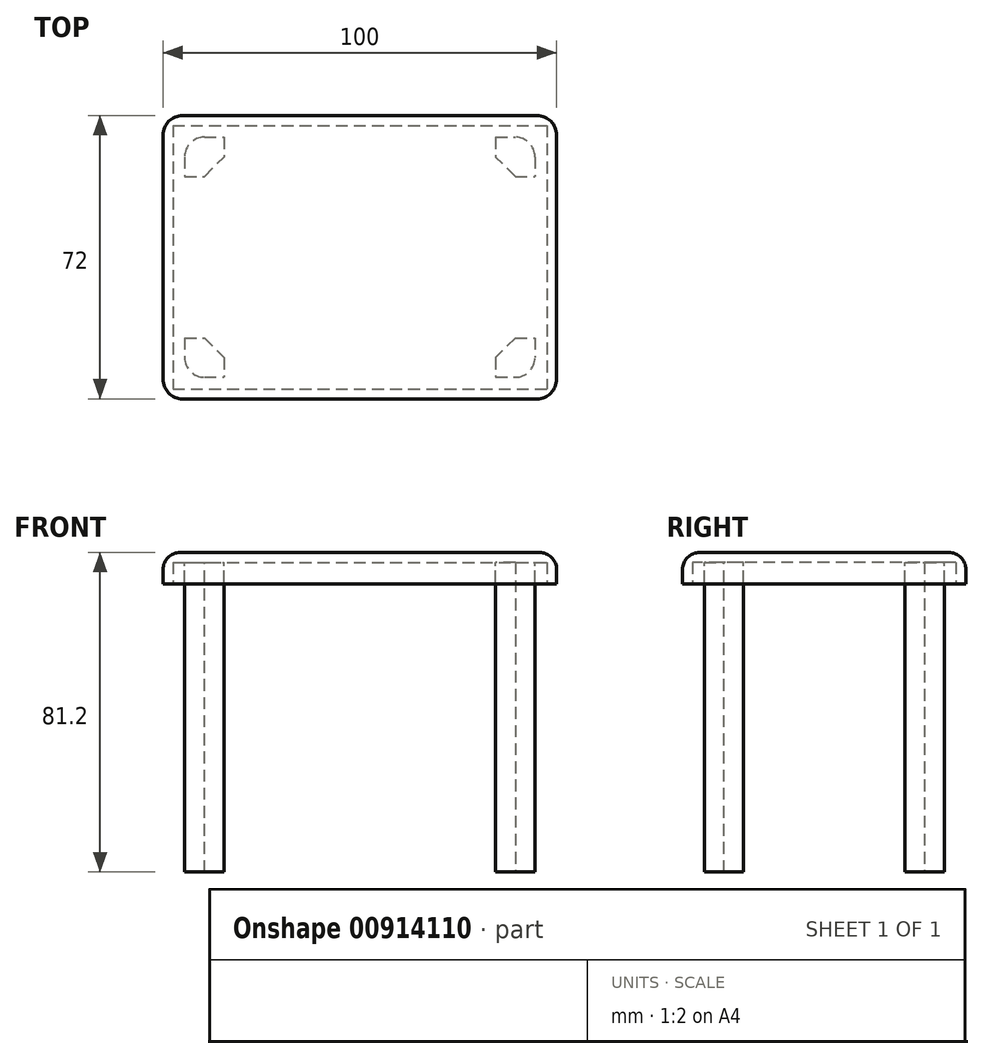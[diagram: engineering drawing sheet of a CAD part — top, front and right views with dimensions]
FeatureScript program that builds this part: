
annotation { "Feature Type Name" : "Feature", "Feature Type Description" : "" }
export const myFeature = defineFeature(function(context is Context, id is Id, definition is map)
    precondition{}
    {
        {
            var Q0;
            Q0=qCreatedBy(makeId("Top.planeOp"),FACE);
            var sketch = newSketch(context, id + "F0", { "sketchPlane" : qUnion([Q0])});
            skLineSegment(sketch, "E0.bottom", {"start": v(-50, 36) * mm, "end": v(50, 36) * mm});
            skLineSegment(sketch, "E0.top", {"start": v(-50, -36) * mm, "end": v(50, -36) * mm});
            skLineSegment(sketch, "E0.left", {"start": v(-50, 36) * mm, "end": v(-50, -36) * mm});
            skLineSegment(sketch, "E0.right", {"start": v(50, 36) * mm, "end": v(50, -36) * mm});
            skLineSegment(sketch, "E1.bottom", {"start": v(-63.65, 0) * mm, "end": v(70, 0) * mm, "construction": true});
            skLineSegment(sketch, "E1.top", {"start": v(-63.65, 0) * mm, "end": v(70, 0) * mm, "construction": true});
            skLineSegment(sketch, "E1.left", {"start": v(-63.65, 0) * mm, "end": v(-63.65, 0) * mm});
            skLineSegment(sketch, "E1.right", {"start": v(70, 0) * mm, "end": v(70, 0) * mm});
            skSolve(sketch);
        }
        {
            var Q0;
            Q0=makeQuery(id+"F0.imprint","IMPRINT",FACE,{"disambiguationData":[TD([[makeQuery(id+"F0.imprint","IMPRINT",EDGE,{"derivedFrom":sQuery(id+"F0.wireOp",EDGE,"E0.bottom")}),-1.0]])]});
            extrude(context, id + "F1", {"entities" : qUnion([Q0]), "depth" : 8 * mm, "offsetDistance" : 25 * mm});
        }
        {
            var Q0;
            Q0=makeQuery(id+"F1.opExtrude","CAP_FACE",FACE,{"disambiguationData":[OSD([sQuery(id+"F0.wireOp",EDGE,"E0.bottom"),sQuery(id+"F0.wireOp",EDGE,"E0.top"),sQuery(id+"F0.wireOp",EDGE,"E0.left"),sQuery(id+"F0.wireOp",EDGE,"E0.right")])],"isStart":true});
            shell(context, id + "F2", {"entities" : qUnion([Q0]), "thickness" : 2.5 * mm});
        }
        {
            var Q0;
            Q0=makeQuery(id+"F2.opShell","OFFSET_FACE",FACE,{"disambiguationData":[OSD([sQuery(id+"F0.wireOp",EDGE,"E0.bottom"),sQuery(id+"F0.wireOp",EDGE,"E0.top"),sQuery(id+"F0.wireOp",EDGE,"E0.left"),sQuery(id+"F0.wireOp",EDGE,"E0.right")])]});
            var sketch = newSketch(context, id + "F3", { "sketchPlane" : qUnion([Q0])});
            skLineSegment(sketch, "E2.bottom", {"start": v(-44.5, -30.5) * mm, "end": v(-34.5, -30.5) * mm});
            skLineSegment(sketch, "E2.top", {"start": v(-44.5, -20.5) * mm, "end": v(-34.5, -20.5) * mm});
            skLineSegment(sketch, "E2.left", {"start": v(-44.5, -30.5) * mm, "end": v(-44.5, -20.5) * mm});
            skLineSegment(sketch, "E2.right", {"start": v(-34.5, -30.5) * mm, "end": v(-34.5, -20.5) * mm});
            skLineSegment(sketch, "E3.bottom", {"start": v(-44.5, 20.5) * mm, "end": v(-34.5, 20.5) * mm});
            skLineSegment(sketch, "E3.top", {"start": v(-44.5, 30.5) * mm, "end": v(-34.5, 30.5) * mm});
            skLineSegment(sketch, "E3.left", {"start": v(-44.5, 20.5) * mm, "end": v(-44.5, 30.5) * mm});
            skLineSegment(sketch, "E3.right", {"start": v(-34.5, 20.5) * mm, "end": v(-34.5, 30.5) * mm});
            skLineSegment(sketch, "E4.bottom", {"start": v(34.5, -30.5) * mm, "end": v(44.5, -30.5) * mm});
            skLineSegment(sketch, "E4.top", {"start": v(34.5, -20.5) * mm, "end": v(44.5, -20.5) * mm});
            skLineSegment(sketch, "E4.left", {"start": v(34.5, -30.5) * mm, "end": v(34.5, -20.5) * mm});
            skLineSegment(sketch, "E4.right", {"start": v(44.5, -30.5) * mm, "end": v(44.5, -20.5) * mm});
            skLineSegment(sketch, "E5.bottom", {"start": v(34.5, 20.5) * mm, "end": v(44.5, 20.5) * mm});
            skLineSegment(sketch, "E5.top", {"start": v(34.5, 30.5) * mm, "end": v(44.5, 30.5) * mm});
            skLineSegment(sketch, "E5.left", {"start": v(34.5, 20.5) * mm, "end": v(34.5, 30.5) * mm});
            skLineSegment(sketch, "E5.right", {"start": v(44.5, 20.5) * mm, "end": v(44.5, 30.5) * mm});
            skSolve(sketch);
        }
        {
            var Q0;
            Q0=makeQuery(id+"F3.imprint","IMPRINT",FACE,{"disambiguationData":[TD([[makeQuery(id+"F3.imprint","IMPRINT",EDGE,{"derivedFrom":sQuery(id+"F3.wireOp",EDGE,"E2.bottom")}),1.0]])]});
            var Q1;
            Q1=makeQuery(id+"F3.imprint","IMPRINT",FACE,{"disambiguationData":[TD([[makeQuery(id+"F3.imprint","IMPRINT",EDGE,{"derivedFrom":sQuery(id+"F3.wireOp",EDGE,"E4.bottom")}),1.0]])]});
            var Q2;
            Q2=makeQuery(id+"F3.imprint","IMPRINT",FACE,{"disambiguationData":[TD([[makeQuery(id+"F3.imprint","IMPRINT",EDGE,{"derivedFrom":sQuery(id+"F3.wireOp",EDGE,"E5.bottom")}),1.0]])]});
            var Q3;
            Q3=makeQuery(id+"F3.imprint","IMPRINT",FACE,{"disambiguationData":[TD([[makeQuery(id+"F3.imprint","IMPRINT",EDGE,{"derivedFrom":sQuery(id+"F3.wireOp",EDGE,"E3.bottom")}),1.0]])]});
            extrude(context, id + "F4", {"entities" : qUnion([Q0, Q1, Q2, Q3]), "operationType" : NewBodyOperationType.ADD, "depth" : 78.7 * mm, "offsetDistance" : 25 * mm});
        }
        {
            var Q0;
            Q0=makeQuery(id+"F1.opExtrude","CAP_EDGE",EDGE,{"disambiguationData":[OSD([sQuery(id+"F0.wireOp",EDGE,"E0.left")])],"isStart":false});
            var Q1;
            Q1=makeQuery(id+"F1.opExtrude","CAP_EDGE",EDGE,{"disambiguationData":[OSD([sQuery(id+"F0.wireOp",EDGE,"E0.top")])],"isStart":false});
            var Q2;
            Q2=makeQuery(id+"F1.opExtrude","CAP_EDGE",EDGE,{"disambiguationData":[OSD([sQuery(id+"F0.wireOp",EDGE,"E0.right")])],"isStart":false});
            var Q3;
            Q3=makeQuery(id+"F1.opExtrude","CAP_EDGE",EDGE,{"disambiguationData":[OSD([sQuery(id+"F0.wireOp",EDGE,"E0.bottom")])],"isStart":false});
            fillet(context, id + "F5", {"entities" : qUnion([Q0, Q1, Q2, Q3]), "radius" : 4.35 * mm, "tangentPropagation" : true, "allowEdgeOverflow" : false});
        }
        {
            var Q0;
            Q0=makeQuery(id+"F4.opExtrude","SWEPT_EDGE",EDGE,{"disambiguationData":[OSD([sQuery(id+"F3.wireOp",EDGE,"E3.top"),sQuery(id+"F3.wireOp",EDGE,"E3.left")])]});
            fillet(context, id + "F6", {"entities" : qUnion([Q0]), "radius" : 5 * mm, "tangentPropagation" : true, "allowEdgeOverflow" : false});
        }
        {
            var Q0;
            Q0=makeQuery(id+"F1.opExtrude","SWEPT_EDGE",EDGE,{"disambiguationData":[OSD([sQuery(id+"F0.wireOp",EDGE,"E0.top"),sQuery(id+"F0.wireOp",EDGE,"E0.left")])]});
            var Q1;
            Q1=makeQuery(id+"F1.opExtrude","SWEPT_EDGE",EDGE,{"disambiguationData":[OSD([sQuery(id+"F0.wireOp",EDGE,"E0.bottom"),sQuery(id+"F0.wireOp",EDGE,"E0.left")])]});
            var Q2;
            Q2=makeQuery(id+"F1.opExtrude","SWEPT_EDGE",EDGE,{"disambiguationData":[OSD([sQuery(id+"F0.wireOp",EDGE,"E0.bottom"),sQuery(id+"F0.wireOp",EDGE,"E0.right")])]});
            var Q3;
            Q3=makeQuery(id+"F4.opExtrude","SWEPT_EDGE",EDGE,{"disambiguationData":[OSD([sQuery(id+"F3.wireOp",EDGE,"E5.top"),sQuery(id+"F3.wireOp",EDGE,"E5.right")])]});
            var Q4;
            Q4=makeQuery(id+"F4.opExtrude","SWEPT_EDGE",EDGE,{"disambiguationData":[OSD([sQuery(id+"F3.wireOp",EDGE,"E4.bottom"),sQuery(id+"F3.wireOp",EDGE,"E4.right")])]});
            var Q5;
            Q5=makeQuery(id+"F4.opExtrude","SWEPT_EDGE",EDGE,{"disambiguationData":[OSD([sQuery(id+"F3.wireOp",EDGE,"E2.bottom"),sQuery(id+"F3.wireOp",EDGE,"E2.left")])]});
            fillet(context, id + "F7", {"entities" : qUnion([Q0, Q1, Q2, Q3, Q4, Q5]), "radius" : 5 * mm, "tangentPropagation" : true, "allowEdgeOverflow" : false});
        }
        {
            var Q0;
            Q0=makeQuery(id+"F4.opExtrude","SWEPT_EDGE",EDGE,{"disambiguationData":[OSD([sQuery(id+"F3.wireOp",EDGE,"E3.bottom"),sQuery(id+"F3.wireOp",EDGE,"E3.right")])]});
            var Q1;
            Q1=makeQuery(id+"F4.opExtrude","SWEPT_EDGE",EDGE,{"disambiguationData":[OSD([sQuery(id+"F3.wireOp",EDGE,"E2.top"),sQuery(id+"F3.wireOp",EDGE,"E2.right")])]});
            var Q2;
            Q2=makeQuery(id+"F4.opExtrude","SWEPT_EDGE",EDGE,{"disambiguationData":[OSD([sQuery(id+"F3.wireOp",EDGE,"E4.top"),sQuery(id+"F3.wireOp",EDGE,"E4.left")])]});
            var Q3;
            Q3=makeQuery(id+"F4.opExtrude","SWEPT_EDGE",EDGE,{"disambiguationData":[OSD([sQuery(id+"F3.wireOp",EDGE,"E5.bottom"),sQuery(id+"F3.wireOp",EDGE,"E5.left")])]});
            chamfer(context, id + "F8", {"entities" : qUnion([Q0, Q1, Q2, Q3]), "width" : 5 * mm, "tangentPropagation" : true});
        }
        {
            var Q0;
            Q0=makeQuery(id+"F1.opExtrude","SWEPT_EDGE",EDGE,{"disambiguationData":[OSD([sQuery(id+"F0.wireOp",EDGE,"E0.top"),sQuery(id+"F0.wireOp",EDGE,"E0.right")])]});
            fillet(context, id + "F9", {"entities" : qUnion([Q0]), "radius" : 5 * mm, "tangentPropagation" : true, "allowEdgeOverflow" : false});
        }
    });
